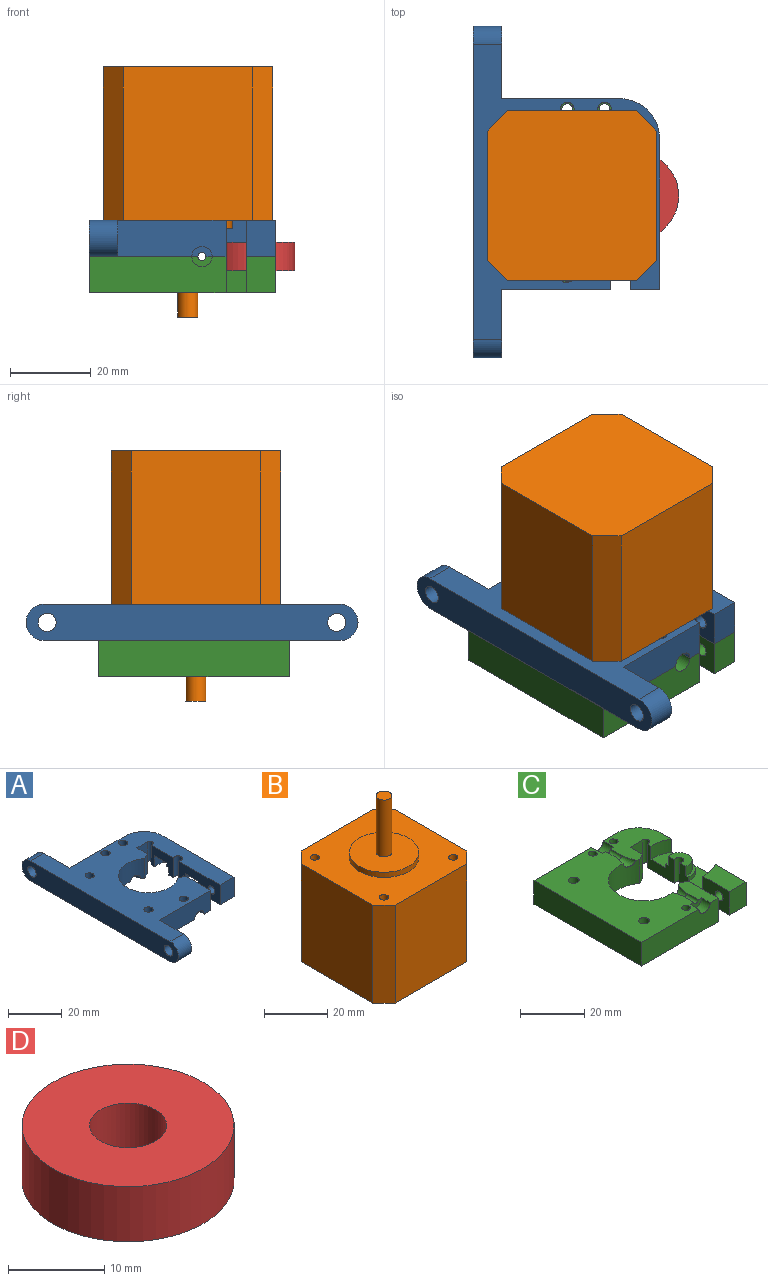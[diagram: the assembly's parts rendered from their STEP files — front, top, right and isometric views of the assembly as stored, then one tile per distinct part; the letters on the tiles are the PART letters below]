
ASSEMBLY  parts=4 mates=3
PART A: 51 faces, bbox 46.2x82.3x9 mm
  f0: plane 11.82x9mm, normal (-1,0,0), area 70mm2, adj f4,f7,f15,f21,f25,f26,f28,f29
  f1: plane 21.81x9mm, normal (-1,0,0), area 150.8mm2, adj f7,f16,f20,f21,f26,f27,f28,f29
  f2: plane 73.31x26.93mm, normal (0,0,-1), area 1154.6mm2, adj f5,f10,f11,f12,f17,f19,f23,f24
  f3: plane 14.38x4.98mm, normal (0,0,-1), area 60mm2, adj f5,f8,f12,f35,f36,f37,f38,f49
  f4: plane 17.27x15.32mm, normal (0,0,-1), area 166.9mm2, adj f0,f5,f6,f9,f10,f13,f14,f15
  f5: cylinder r=11.1mm len=22.2mm, axis (0,0,-1), area 432.3mm2, adj f2,f3,f4,f21,f34,f37,f49,f50
  f6: plane 37.28x9mm, normal (1,0,0), area 230.1mm2, adj f4,f16,f20,f21,f22,f25,f27,f28
  f7: plane 8x5.02mm, normal (0,0,-1), area 25.4mm2, adj f0,f1,f29,f42
  f8: plane 13.04x9mm, normal (1,0,0), area 111.2mm2, adj f3,f12,f21,f40,f49
  f9: plane 9x5.51mm, normal (1,0,0), area 49.5mm2, adj f4,f13,f21,f50
  f10: plane 29.2x9mm, normal (0,1,0), area 252.8mm2, adj f2,f4,f21,f22,f33,f44
  f11: plane 82.31x9mm, normal (-1,0,0), area 691.6mm2, adj f2,f21,f45,f46,f47,f48
  f12: plane 26.91x9mm, normal (0,-1,0), area 232.2mm2, adj f2,f3,f8,f21,f38,f43
  f13: plane 9x5.65mm, normal (0,-1,0), area 50.9mm2, adj f4,f9,f14,f21
  f14: cylinder r=1.22mm len=9mm, axis (0,0,1), area 34.6mm2, adj f4,f13,f15,f21
  f15: plane 9x0.65mm, normal (0,1,0), area 5.9mm2, adj f0,f4,f14,f21
  f16: plane 9x7.29mm, normal (0,-1,0), area 65.6mm2, adj f1,f6,f20,f21
  f17: cylinder r=1.7mm len=9mm, axis (0,0,1), area 96.1mm2, adj f2,f21
  f18: cylinder r=1.7mm len=9mm, axis (0,0,1), area 96.1mm2, adj f4,f21
  f19: cylinder r=1.7mm len=9mm, axis (0,0,1), area 96.1mm2, adj f2,f21
  f20: plane 13.53x7.29mm, normal (0,0,-1), area 88.9mm2, adj f1,f6,f16,f27
  f21: plane 73.31x46.2mm, normal (0,0,1), area 1708.8mm2, adj f0,f1,f5,f6,f8,f9,f10,f11
  f22: cylinder r=10mm len=10mm, axis (0,0,1), area 141.4mm2, adj f4,f6,f10,f21
  f23: cylinder r=1.7mm len=9mm, axis (0,0,-1), area 96.1mm2, adj f2,f21
  f24: cylinder r=1.7mm len=9mm, axis (0,0,-1), area 96.1mm2, adj f2,f21
  f25: cylinder r=11.5mm len=7.29mm, axis (0,0,-1), area 38.3mm2, adj f0,f4,f6,f28
  f26: cylinder r=5mm len=10mm, axis (0,0,-1), area 26.6mm2, adj f0,f1,f28,f30
  f27: cylinder r=11.5mm len=7.29mm, axis (0,0,-1), area 38.3mm2, adj f1,f6,f20,f28
  f28: plane 23x7.29mm, normal (0,0,-1), area 110.8mm2, adj f0,f1,f6,f25,f26,f27
  f29: cylinder r=4mm len=8mm, axis (0,0,-1), area 51.2mm2, adj f0,f1,f7,f30
  f30: plane 10x6.02mm, normal (0,0,-1), area 16.2mm2, adj f0,f1,f26,f29
  f31: plane 5.04x2.52mm, normal (0,1,0), area 8.4mm2, adj f2,f4,f32,f33
  f32: cylinder r=1mm len=4.98mm, axis (0,-1,0), area 15.6mm2, adj f2,f4,f31,f34
  f33: cylinder r=2.52mm len=5.04mm, axis (0,-1,0), area 37.6mm2, adj f2,f4,f10,f31
  f34: cone r=1mm half-angle=13.3deg, axis (0,-1,0), area 19mm2, adj f2,f4,f5,f32
  f35: cylinder r=1mm len=4.98mm, axis (0,-1,0), area 15.6mm2, adj f2,f3,f36,f37
  f36: plane 5.04x2.52mm, normal (0,-1,0), area 8.4mm2, adj f2,f3,f35,f38
  f37: cone r=1mm half-angle=13.3deg, axis (0,1,0), area 19mm2, adj f2,f3,f5,f35
  f38: cylinder r=2.52mm len=5.04mm, axis (0,-1,0), area 30.1mm2, adj f2,f3,f12,f36
  f39: plane 2.8x2.8mm, normal (1,0,0), area 6.2mm2, adj f40
  f40: cylinder r=1.4mm len=7.71mm, axis (1,0,0), area 67.8mm2, adj f8,f39
  f41: cylinder r=1.7mm len=7.29mm, axis (1,0,0), area 77.9mm2, adj f1,f6
  f42: cylinder r=1.7mm len=9mm, axis (0,0,-1), area 67.7mm2, adj f0,f1,f7,f21
  f43: plane 17.03x9mm, normal (1,0,0), area 128.7mm2, adj f2,f12,f21,f45,f47
  f44: plane 18x9mm, normal (1,0,0), area 137.4mm2, adj f2,f10,f21,f46,f48
  f45: cylinder r=2.25mm len=7mm, axis (1,0,0), area 99mm2, adj f11,f43
  f46: cylinder r=2.25mm len=7mm, axis (1,0,0), area 99mm2, adj f11,f44
  f47: cylinder r=4.5mm len=9mm, axis (1,0,0), area 99mm2, adj f2,f11,f21,f43
  f48: cylinder r=4.5mm len=9mm, axis (-1,0,0), area 99mm2, adj f2,f11,f21,f44
  f49: plane 9x2.71mm, normal (0.44,0.9,0), area 27.2mm2, adj f3,f5,f8,f21
  f50: plane 9x2.71mm, normal (0.44,-0.9,0), area 27.2mm2, adj f4,f5,f9,f21
PART B: 22 faces, bbox 42x42x62 mm
  f0: plane 38x32mm, normal (-1,0,0), area 1216mm2, adj f4,f5,f8,f9
  f1: plane 38x32mm, normal (0,-1,0), area 1216mm2, adj f4,f5,f7,f9
  f2: plane 38x32mm, normal (1,0,0), area 1216mm2, adj f4,f5,f6,f7
  f3: plane 38x32mm, normal (0,1,0), area 1216mm2, adj f4,f5,f6,f8
  f4: plane 42x42mm, normal (0,0,1), area 1305.6mm2, adj f0,f1,f2,f3,f6,f7,f8,f9
  f5: plane 42x42mm, normal (0,0,-1), area 1714mm2, adj f0,f1,f2,f3,f6,f7,f8,f9
  f6: plane 38x5mm, normal (0.71,0.71,0), area 268.7mm2, adj f2,f3,f4,f5
  f7: plane 38x5mm, normal (0.71,-0.71,0), area 268.7mm2, adj f1,f2,f4,f5
  f8: plane 38x5mm, normal (-0.71,0.71,0), area 268.7mm2, adj f0,f3,f4,f5
  f9: plane 38x5mm, normal (-0.71,-0.71,0), area 268.7mm2, adj f0,f1,f4,f5
  f10: cylinder r=11mm len=22mm, axis (0,0,-1), area 138.2mm2, adj f4,f11
  f11: plane 22x22mm, normal (0,0,1), area 360.5mm2, adj f10,f12
  f12: cylinder r=2.5mm len=22mm, axis (0,0,-1), area 345.6mm2, adj f11,f13
  f13: plane 5x5mm, normal (0,0,1), area 19.6mm2, adj f12
  f14: cylinder r=1.5mm len=25mm, axis (0,0,1), area 235.6mm2, adj f4,f15
  f15: plane 3x3mm, normal (0,0,1), area 7.1mm2, adj f14
  f16: cylinder r=1.5mm len=25mm, axis (0,0,1), area 235.6mm2, adj f4,f17
  f17: plane 3x3mm, normal (0,0,1), area 7.1mm2, adj f16
  f18: cylinder r=1.5mm len=25mm, axis (0,0,1), area 235.6mm2, adj f4,f19
  f19: plane 3x3mm, normal (0,0,1), area 7.1mm2, adj f18
  f20: cylinder r=1.5mm len=25mm, axis (0,0,1), area 235.6mm2, adj f4,f21
  f21: plane 3x3mm, normal (0,0,1), area 7.1mm2, adj f20
PART C: 45 faces, bbox 46.2x47.3x9 mm
  f0: plane 12.22x9mm, normal (-1,0,0), area 73.6mm2, adj f3,f6,f7,f15,f22,f25,f27,f28
  f1: plane 47.28x26.93mm, normal (0,0,1), area 979.1mm2, adj f4,f9,f10,f11,f18,f20,f23,f24
  f2: plane 14.38x4.98mm, normal (0,0,1), area 60mm2, adj f4,f8,f11,f34,f35,f36,f37,f44
  f3: plane 17.27x15.32mm, normal (0,0,1), area 170.2mm2, adj f0,f4,f9,f12,f13,f14,f15,f17
  f4: cylinder r=11.1mm len=22.2mm, axis (0,0,1), area 432.3mm2, adj f1,f2,f3,f22,f33,f34,f43,f44
  f5: plane 22.21x9mm, normal (-1,0,0), area 154.4mm2, adj f6,f7,f16,f21,f22,f26,f27,f28
  f6: plane 8x5.02mm, normal (0,0,1), area 27.5mm2, adj f0,f5,f28,f42
  f7: cylinder r=5mm len=10mm, axis (0,0,1), area 26.6mm2, adj f0,f5,f27,f29
  f8: plane 13.04x9mm, normal (1,0,0), area 111.2mm2, adj f2,f11,f22,f39,f44
  f9: plane 36.2x9mm, normal (0,1,0), area 315.8mm2, adj f1,f3,f10,f22,f30,f38
  f10: plane 47.28x9mm, normal (-1,0,0), area 425.5mm2, adj f1,f9,f11,f22
  f11: plane 33.91x9mm, normal (0,-1,0), area 295.2mm2, adj f1,f2,f8,f10,f22,f37
  f12: plane 9x5.51mm, normal (1,0,0), area 49.5mm2, adj f3,f13,f22,f43
  f13: plane 9x5.65mm, normal (0,-1,0), area 50.9mm2, adj f3,f12,f14,f22
  f14: cylinder r=1.22mm len=9mm, axis (0,0,-1), area 34.6mm2, adj f3,f13,f15,f22
  f15: plane 9x0.65mm, normal (0,1,0), area 5.9mm2, adj f0,f3,f14,f22
  f16: plane 9x7.29mm, normal (0,-1,0), area 65.6mm2, adj f5,f19,f21,f22
  f17: cylinder r=1.35mm len=9mm, axis (0,0,-1), area 76.3mm2, adj f3,f22
  f18: cylinder r=1.35mm len=9mm, axis (0,0,-1), area 76.3mm2, adj f1,f22
  f19: plane 37.28x9mm, normal (1,0,0), area 230.1mm2, adj f3,f16,f21,f22,f25,f26,f27,f38
  f20: cylinder r=1.35mm len=9mm, axis (0,0,-1), area 76.3mm2, adj f1,f22
  f21: plane 13.53x7.29mm, normal (0,0,1), area 88.9mm2, adj f5,f16,f19,f26
  f22: plane 47.28x46.2mm, normal (0,0,-1), area 1538.8mm2, adj f0,f4,f5,f8,f9,f10,f11,f12
  f23: cylinder r=1.7mm len=9mm, axis (0,0,1), area 96.1mm2, adj f1,f22
  f24: cylinder r=1.7mm len=9mm, axis (0,0,1), area 96.1mm2, adj f1,f22
  f25: cylinder r=11.5mm len=7.29mm, axis (0,0,1), area 38.3mm2, adj f0,f3,f19,f27
  f26: cylinder r=11.5mm len=7.29mm, axis (0,0,1), area 38.3mm2, adj f5,f19,f21,f27
  f27: plane 23x7.29mm, normal (0,0,1), area 110.8mm2, adj f0,f5,f7,f19,f25,f26
  f28: cylinder r=4mm len=8mm, axis (0,0,1), area 51.2mm2, adj f0,f5,f6,f29
  f29: plane 10x6.02mm, normal (0,0,1), area 16.2mm2, adj f0,f5,f7,f28
  f30: cylinder r=2.52mm len=5.04mm, axis (0,-1,0), area 37.6mm2, adj f1,f3,f9,f31
  f31: plane 5.04x2.52mm, normal (0,1,0), area 8.4mm2, adj f1,f3,f30,f32
  f32: cylinder r=1mm len=4.98mm, axis (0,-1,0), area 15.6mm2, adj f1,f3,f31,f33
  f33: cone r=1mm half-angle=13.3deg, axis (0,-1,0), area 19mm2, adj f1,f3,f4,f32
  f34: cone r=1mm half-angle=13.3deg, axis (0,1,0), area 19mm2, adj f1,f2,f4,f35
  f35: cylinder r=1mm len=4.98mm, axis (0,-1,0), area 15.6mm2, adj f1,f2,f34,f36
  f36: plane 5.04x2.52mm, normal (0,-1,0), area 8.4mm2, adj f1,f2,f35,f37
  f37: cylinder r=2.52mm len=5.04mm, axis (0,-1,0), area 30.1mm2, adj f1,f2,f11,f36
  f38: cylinder r=10mm len=10mm, axis (0,0,-1), area 141.4mm2, adj f3,f9,f19,f22
  f39: cylinder r=1.4mm len=7.71mm, axis (1,0,0), area 67.8mm2, adj f8,f40
  f40: plane 2.8x2.8mm, normal (1,0,0), area 6.2mm2, adj f39
  f41: cylinder r=1.7mm len=7.29mm, axis (1,0,0), area 77.9mm2, adj f5,f19
  f42: cylinder r=1.4mm len=9mm, axis (0,0,1), area 60.1mm2, adj f0,f5,f6,f22
  f43: plane 9x2.71mm, normal (0.44,-0.9,0), area 27.2mm2, adj f3,f4,f12,f22
  f44: plane 9x2.71mm, normal (0.44,0.9,0), area 27.2mm2, adj f2,f4,f8,f22
PART D: 4 faces, bbox 22x22x7 mm
  f0: cylinder r=4mm len=8mm, axis (0,0,-1), area 175.9mm2, adj f2,f3
  f1: cylinder r=11mm len=22mm, axis (0,0,-1), area 483.8mm2, adj f2,f3
  f2: plane 22x22mm, normal (0,0,1), area 329.9mm2, adj f0,f1
  f3: plane 22x22mm, normal (0,0,-1), area 329.9mm2, adj f0,f1
PLACE A t=(-37.06,-1.17,34.2)mm
PLACE B rot(axis=(0.71,-0.71,0),180deg) t=(-16.06,25.66,90.2)mm
PLACE C t=(-37.06,-1.17,34.2)mm
PLACE D t=(-21.56,4.66,39.7)mm
MATE fastened D.f0 <-> C.f7  axis (0,0,-1) through (-21.56,4.66,39.7)mm
MATE fastened B.f20 <-> A.f24  axis (0,0,-1) through (-52.56,20.16,52.2)mm
MATE fastened D.f0 <-> A.f25  axis (0,0,1) through (-21.56,4.66,46.7)mm
